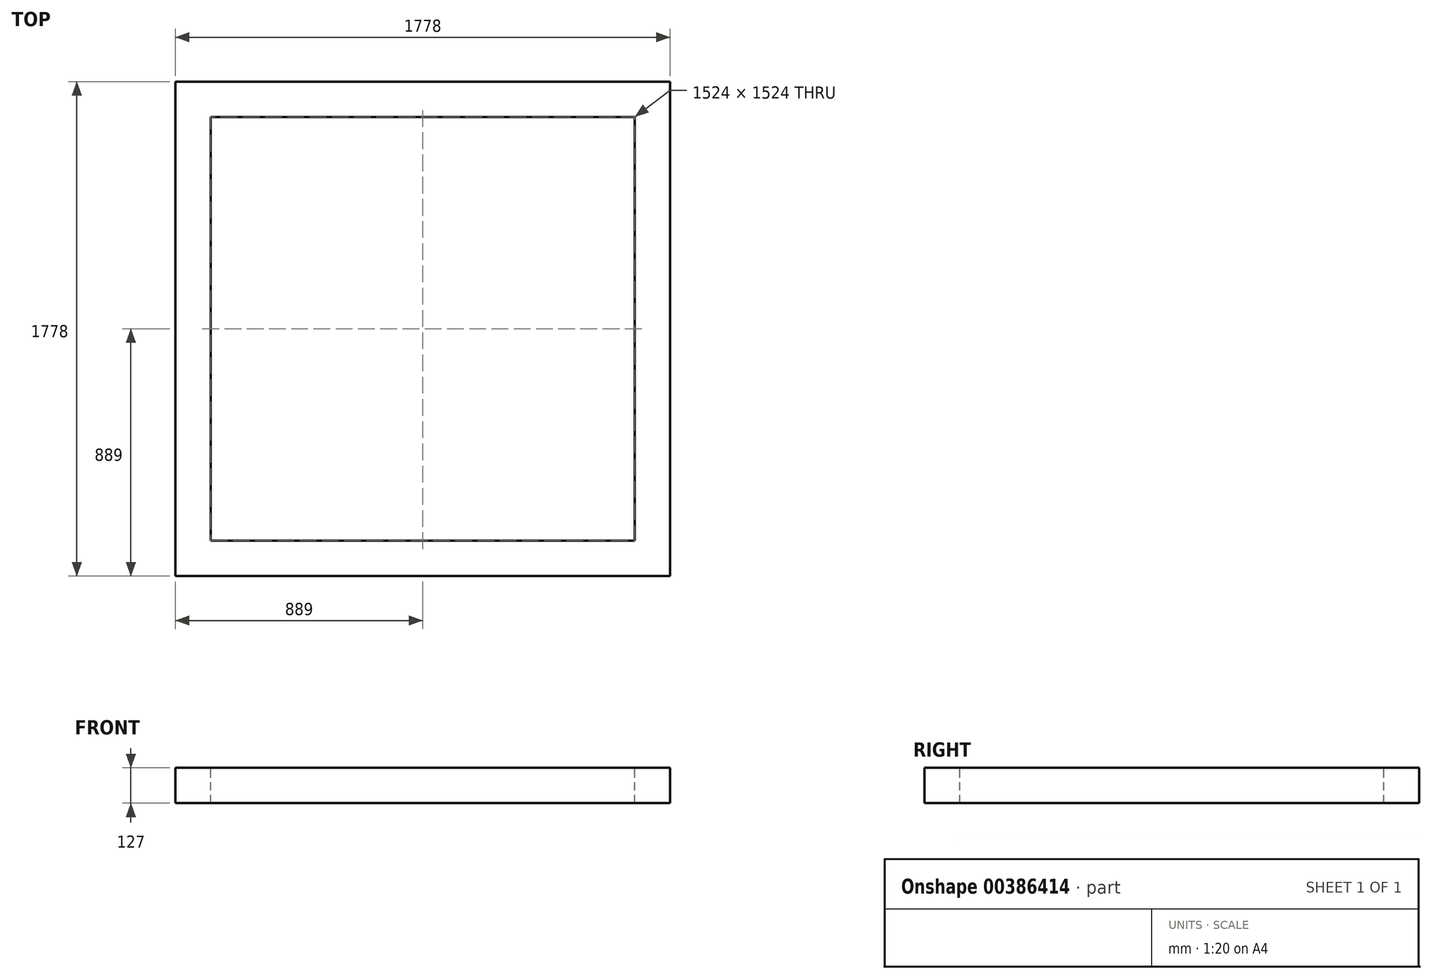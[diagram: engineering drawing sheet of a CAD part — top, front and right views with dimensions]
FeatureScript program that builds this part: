
annotation { "Feature Type Name" : "Feature", "Feature Type Description" : "" }
export const myFeature = defineFeature(function(context is Context, id is Id, definition is map)
    precondition{}
    {
        {
            var Q0;
            Q0=qCreatedBy(makeId("Top.planeOp"),FACE);
            var sketch = newSketch(context, id + "F0", { "sketchPlane" : qUnion([Q0])});
            skLineSegment(sketch, "E0.bottom", {"start": v(-889, 889) * mm, "end": v(889, 889) * mm});
            skLineSegment(sketch, "E0.top", {"start": v(-889, -889) * mm, "end": v(889, -889) * mm});
            skLineSegment(sketch, "E0.left", {"start": v(-889, 889) * mm, "end": v(-889, -889) * mm});
            skLineSegment(sketch, "E0.right", {"start": v(889, 889) * mm, "end": v(889, -889) * mm});
            skPoint(sketch, "E0.middle", {"position": v(0, 0) * mm});
            skLineSegment(sketch, "E1.0", {"start": v(-762, 762) * mm, "end": v(762, 762) * mm});
            skLineSegment(sketch, "E1.1", {"start": v(-762, 762) * mm, "end": v(-762, -762) * mm});
            skLineSegment(sketch, "E1.2", {"start": v(-762, -762) * mm, "end": v(762, -762) * mm});
            skLineSegment(sketch, "E1.3", {"start": v(762, 762) * mm, "end": v(762, -762) * mm});
            skSolve(sketch);
        }
        {
            var Q0;
            Q0 = qSketchRegion(id + "F0", true);
            extrude(context, id + "F1", {"entities" : qUnion([Q0]), "oppositeDirection" : true, "depth" : 127 * mm});
        }
    });
